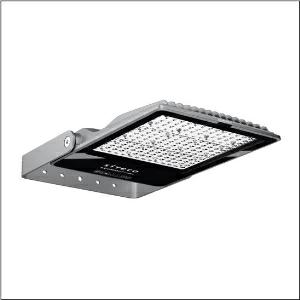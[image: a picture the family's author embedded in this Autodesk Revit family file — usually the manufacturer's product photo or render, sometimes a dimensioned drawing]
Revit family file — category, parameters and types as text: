
# Revit family: sicompact_r__31_midi___pl32_5xa7581d2k23_8dbf
name_source: partatom
category: Lighting Fixtures
units: mm (PartAtom-declared; Revit-internal decimal feet)

## family parameters
Cut with Voids When Loaded = No
Host = Face
Light Source = No
Part Type = Normal
Room Calculation Point = No
Round Connector Dimension = Use Diameter
Shared = No

## types (1)
- SiCompact® 31 midi  PL32 (1 x LED, 27000 lm, 165 W, 4000K)
    Apparent Load = 165 VA
    CIE Flux Codes = 32 69 98 100 100
    Color Rendering = 70
    Color Temperature = 4000K
    Default Elevation = 1800 mm
    Description = SiCompact® 31 midi, floodlight, primary light control with lens, of plastic, of toughened safety glass, transparent, light distribution: PL32, light emission: direct distribution, primary light characteristic: asymmetric, installation type: surface-mounted, LED, High Power LED, rated luminous flux: 27.000lm, luminous efficacy: 164lm/W, light colour: 740, colour temperature: 4000K, control gear: ECG, with cable, 3x 1.5mm², mains connection: 220..240V, AC, 50/60Hz, connection cable pre-assembled, cable length: 2m, rated input power: 165W, of diecast aluminium, specular, metallic grey (RAL 9006), length: 560mm, width: 330mm, height: 62mm, bracket, of sheet steel, coated, metallic grey (RAL 9006), ON/OFF, protection rating (complete): IP66, insulation class (complete): insulation class I (protective earthing), certification: CE, ENEC, impact resistance: IK08, permissible operating ambient temperature: -40..+45°C, packaging unit: 1 piece

Light Distribution: PL32
    Height = 62 mm  [stored 0.203412 ft]
    Lamp = 1 x LED
    Lamp Light Flux = 27000 lm
    Lamp Power = 165 W
    Lamp count = 1
    Length = 560 mm
    Luminous efficacy = 164 lm/W
    Manufacturer = Siteco
    ModVariant = No
    Model = 5XA7581D2K23
    Mounting Place = Wall
    Mounting Type = Surface mounted
    Number of Poles = 1
    OnlyDefault = Yes
    Power Factor = 1
    Product Name = SiCompact® 31 midi | PL32
    Product group = floodlight | wall mounted
    ProductGroupID = 2001
    Protection Class = Protection class I
    Protection Degree = IP 66
    RLX_Detail_Level = 1
    RLX_Emergency_Light_Flux = 0 lm
    RLX_Emergency_Type = 0
    RLX_Emergency_Type_DB = No
    RlxData = <blob elided: 98593 chars, md5=005145f4>
    Socket = socket
    Standby Power = 0 W
    System Light Flux = 27000 lm
    System Power = 165 W
    Type Comments = Product without accessories
    Type Image = l_1006415.jpg
    URL = http://relux.com
    VarID = ---
    Voltage = 0 V
    Weight = 0.00 kg
    Width = 333 mm

note: [stored X ft] marks values corroborated as IEEE doubles in the binary element streams (Revit-internal decimal feet)

## geometry (parser evidence)
native form markers: Blend x4, Sweep x14
no freeform markers — native parametric forms only
